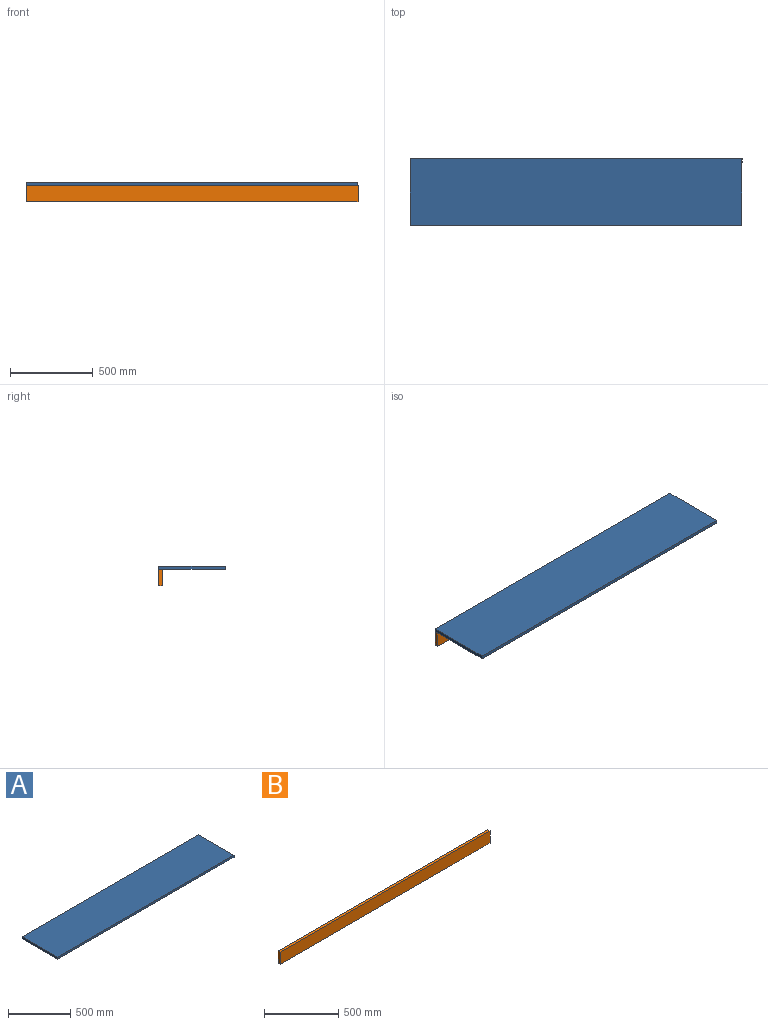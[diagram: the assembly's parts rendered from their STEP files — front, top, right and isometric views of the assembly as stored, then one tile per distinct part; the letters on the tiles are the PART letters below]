
ASSEMBLY  parts=2 mates=1
PART A: 6 faces, bbox 2000x400x20 mm
  f0: plane 2000x20mm, normal (0,1,0), area 40000mm2, adj f1,f3,f4,f5
  f1: plane 400x20mm, normal (-1,0,0), area 8000mm2, adj f0,f2,f4,f5
  f2: plane 2000x20mm, normal (0,-1,0), area 40000mm2, adj f1,f3,f4,f5
  f3: plane 400x20mm, normal (1,0,0), area 8000mm2, adj f0,f2,f4,f5
  f4: plane 2000x400mm, normal (0,0,1), area 800000mm2, adj f0,f1,f2,f3
  f5: plane 2000x400mm, normal (0,0,-1), area 800000mm2, adj f0,f1,f2,f3
PART B: 6 faces, bbox 2000x20x100 mm
  f0: plane 2000x20mm, normal (0,0,1), area 40000mm2, adj f1,f3,f4,f5
  f1: plane 100x20mm, normal (-1,0,0), area 2000mm2, adj f0,f2,f4,f5
  f2: plane 2000x20mm, normal (0,0,-1), area 40000mm2, adj f1,f3,f4,f5
  f3: plane 100x20mm, normal (1,0,0), area 2000mm2, adj f0,f2,f4,f5
  f4: plane 2000x100mm, normal (0,-1,0), area 200000mm2, adj f0,f1,f2,f3
  f5: plane 2000x100mm, normal (0,1,0), area 200000mm2, adj f0,f1,f2,f3
PLACE A t=(1291.82,280.66,17.42)mm
PLACE B t=(1340.31,403.09,17.42)mm
MATE planar B.f0 <-> A.f5  axis (0,0,1) through (285.39,403.09,17.42)mm
